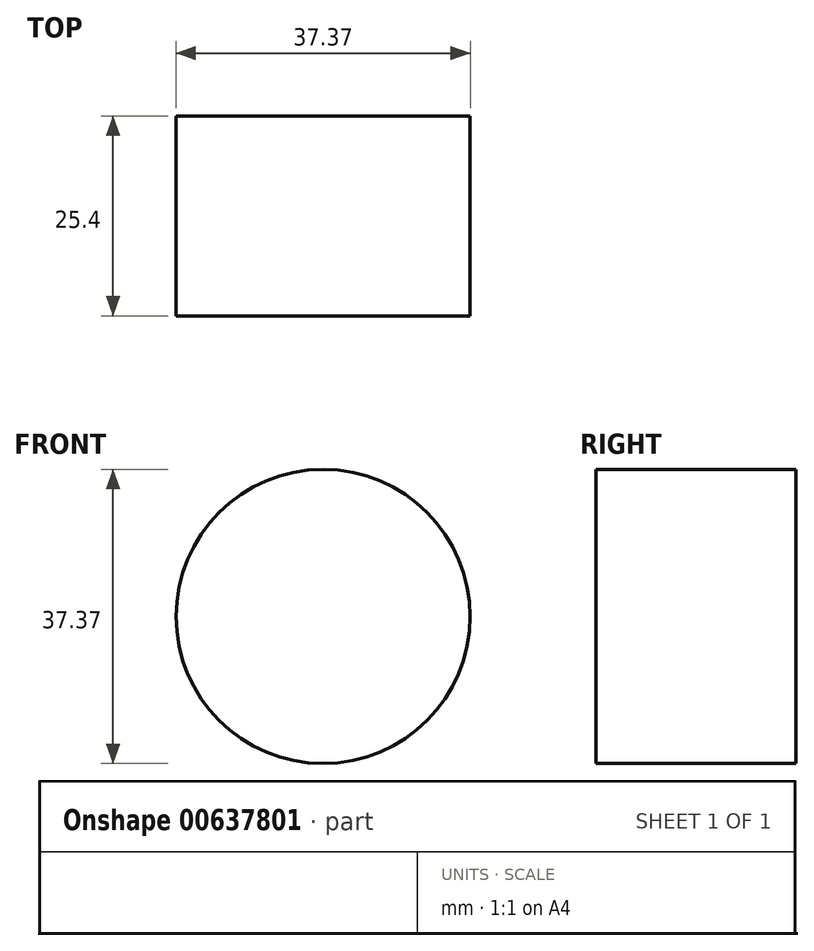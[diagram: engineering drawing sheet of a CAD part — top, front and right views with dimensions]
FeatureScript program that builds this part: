
annotation { "Feature Type Name" : "Feature", "Feature Type Description" : "" }
export const myFeature = defineFeature(function(context is Context, id is Id, definition is map)
    precondition{}
    {
        {
            var Q0;
            Q0=qCreatedBy(makeId("Front.planeOp"),FACE);
            var sketch = newSketch(context, id + "F0", { "sketchPlane" : qUnion([Q0])});
            skCircle(sketch, "E0", {"center": v(27.78, 29.7) * mm, "radius": 18.68 * mm});
            skSolve(sketch);
        }
        {
            var Q0;
            Q0 = qSketchRegion(id + "F0", true);
            extrude(context, id + "F1", {"entities" : qUnion([Q0]), "depth" : 25.4 * mm, "offsetDistance" : 25.4 * mm});
        }
    });
